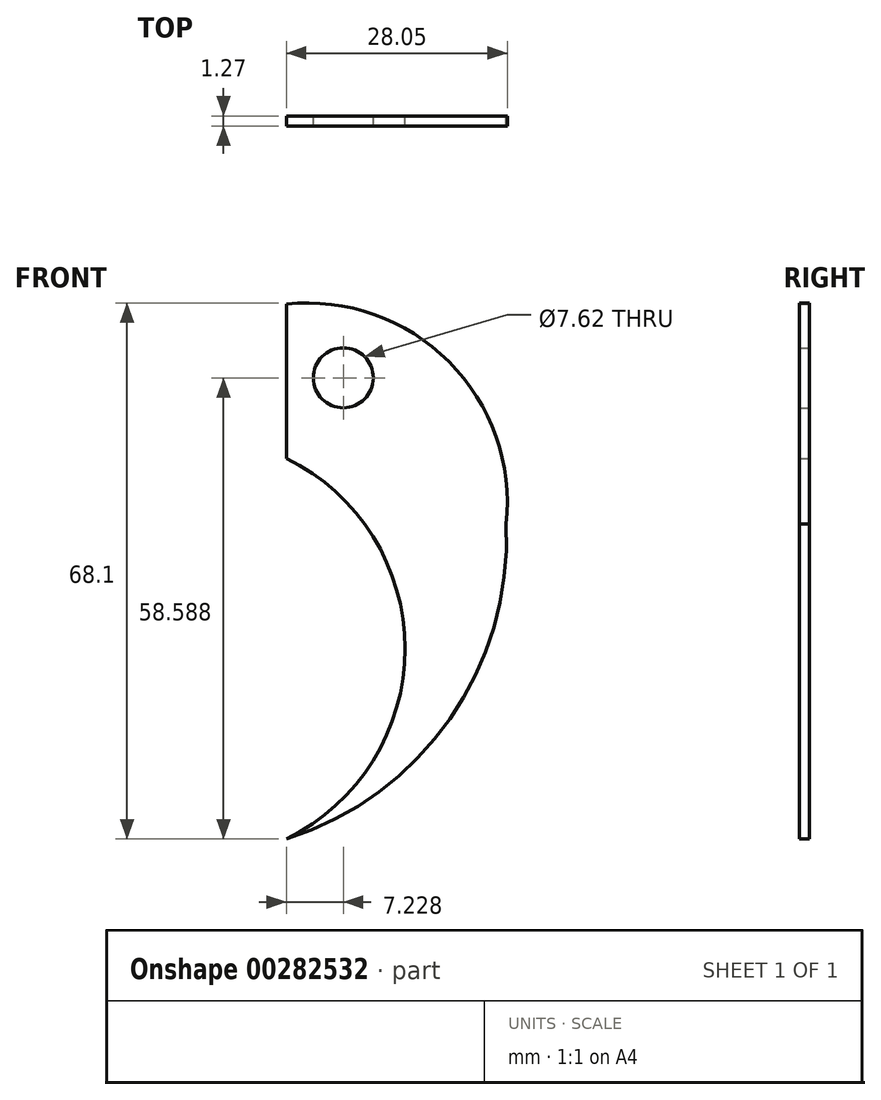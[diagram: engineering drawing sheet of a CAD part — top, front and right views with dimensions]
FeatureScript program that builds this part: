
annotation { "Feature Type Name" : "Feature", "Feature Type Description" : "" }
export const myFeature = defineFeature(function(context is Context, id is Id, definition is map)
    precondition{}
    {
        {
            var Q0;
            Q0=qCreatedBy(makeId("Front.planeOp"),FACE);
            var sketch = newSketch(context, id + "F0", { "sketchPlane" : qUnion([Q0])});
            skArc(sketch, "E0", {"start": v(6.26, -3.5) * mm, "mid": v(-1.01, 17.15) * mm, "end": v(-21.64, 24.46) * mm});
            skArc(sketch, "E1", {"start": v(-21.64, -43.5) * mm, "mid": v(-0.88, -28.24) * mm, "end": v(6.26, -3.5) * mm});
            skArc(sketch, "E2", {"start": v(-21.64, -43.5) * mm, "mid": v(-6.57, -19.32) * mm, "end": v(-21.64, 4.87) * mm});
            skLineSegment(sketch, "E3", {"start": v(-21.64, 24.46) * mm, "end": v(-21.64, 4.87) * mm});
            skCircle(sketch, "E4", {"center": v(-14.41, 15.09) * mm, "radius": 3.81 * mm});
            skSolve(sketch);
        }
        {
            var Q0;
            Q0=makeQuery(id+"F0.imprint","IMPRINT",FACE,{"disambiguationData":[TD([[makeQuery(id+"F0.imprint","IMPRINT",EDGE,{"derivedFrom":sQuery(id+"F0.wireOp",EDGE,"E0")}),1.0]])]});
            extrude(context, id + "F1", {"entities" : qUnion([Q0]), "depth" : 1.27 * mm});
        }
    });
